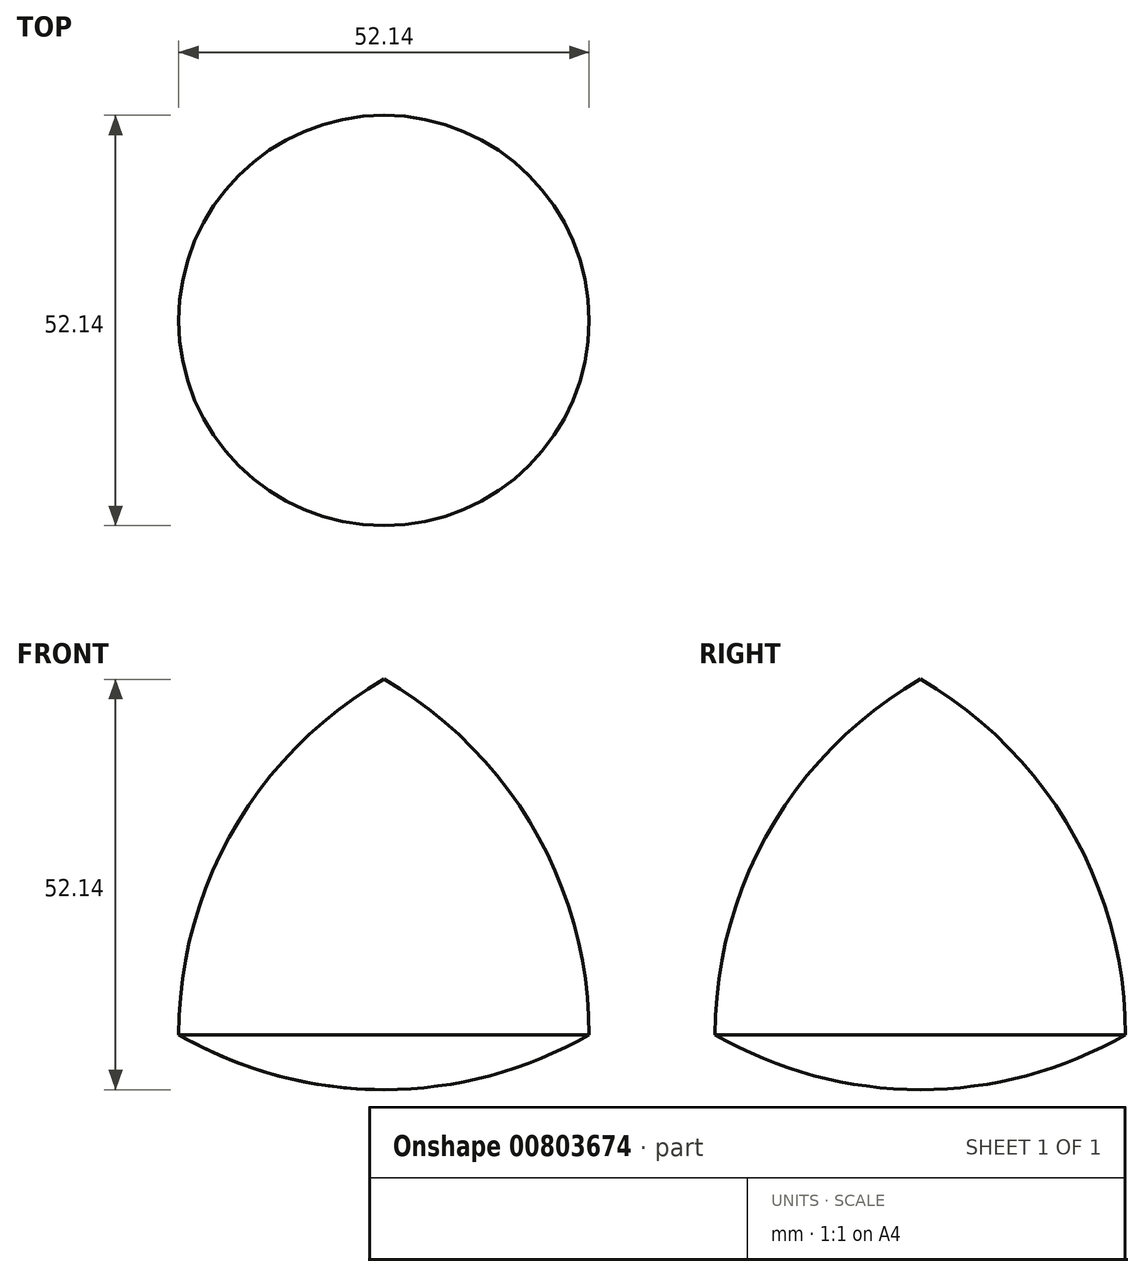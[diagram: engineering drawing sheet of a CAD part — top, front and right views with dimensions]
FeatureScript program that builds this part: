
annotation { "Feature Type Name" : "Feature", "Feature Type Description" : "" }
export const myFeature = defineFeature(function(context is Context, id is Id, definition is map)
    precondition{}
    {
        {
            var Q0;
            Q0=qCreatedBy(makeId("Front.planeOp"),FACE);
            var sketch = newSketch(context, id + "F0", { "sketchPlane" : qUnion([Q0])});
            skLineSegment(sketch, "E0", {"start": v(0, 0) * mm, "end": v(0, 45.15) * mm});
            skLineSegment(sketch, "E1", {"start": v(0, 45.15) * mm, "end": v(26.07, 0) * mm});
            skLineSegment(sketch, "E2", {"start": v(26.07, 0) * mm, "end": v(-26.07, 0) * mm});
            skLineSegment(sketch, "E3", {"start": v(-26.07, 0) * mm, "end": v(0, 45.15) * mm});
            skCircle(sketch, "E4", {"center": v(0, 45.15) * mm, "radius": 52.14 * mm});
            skCircle(sketch, "E5", {"center": v(-26.07, 0) * mm, "radius": 52.14 * mm});
            skCircle(sketch, "E6", {"center": v(26.07, 0) * mm, "radius": 52.14 * mm});
            skLineSegment(sketch, "E7", {"start": v(0, 45.15) * mm, "end": v(0, -6.99) * mm});
            skSolve(sketch);
        }
        {
            var Q0;
            {var subQ0=sQuery(id+"F0.wireOp",EDGE,"E4");var subQ3=sQuery(id+"F0.wireOp",EDGE,"E7");var subQ5=makeQuery(id+"F0.imprint","INTERSECT",VERTEX,{"derivedFrom":[subQ0,subQ3]});Q0=makeQuery(id+"F0.imprint","IMPRINT",FACE,{"disambiguationData":[TD([[makeQuery(id+"F0.imprint","IMPRINT",EDGE,{"disambiguationData":[TD([[subQ5,1.0]])],"derivedFrom":subQ3}),-1.0]])]});}
            var Q1;
            {var subQ1=sQuery(id+"F0.wireOp",EDGE,"E3");Q1=makeQuery(id+"F0.imprint","IMPRINT",FACE,{"disambiguationData":[TD([[makeQuery(id+"F0.imprint","IMPRINT",EDGE,{"derivedFrom":subQ1}),-1.0]])]});}
            var Q2;
            {var subQ0=sQuery(id+"F0.wireOp",EDGE,"E3");Q2=makeQuery(id+"F0.imprint","IMPRINT",FACE,{"disambiguationData":[TD([[makeQuery(id+"F0.imprint","IMPRINT",EDGE,{"derivedFrom":subQ0}),1.0]])]});}
            var Q3;
            Q3=sQuery(id+"F0.wireOp",EDGE,"E7");
            revolve(context, id + "F1", {"surfaceOperationType" : NewSurfaceOperationType.NEW, "entities" : qUnion([Q0, Q1, Q2]), "axis" : qUnion([Q3]), "revolveType" : RevolveType.FULL});
        }
    });
